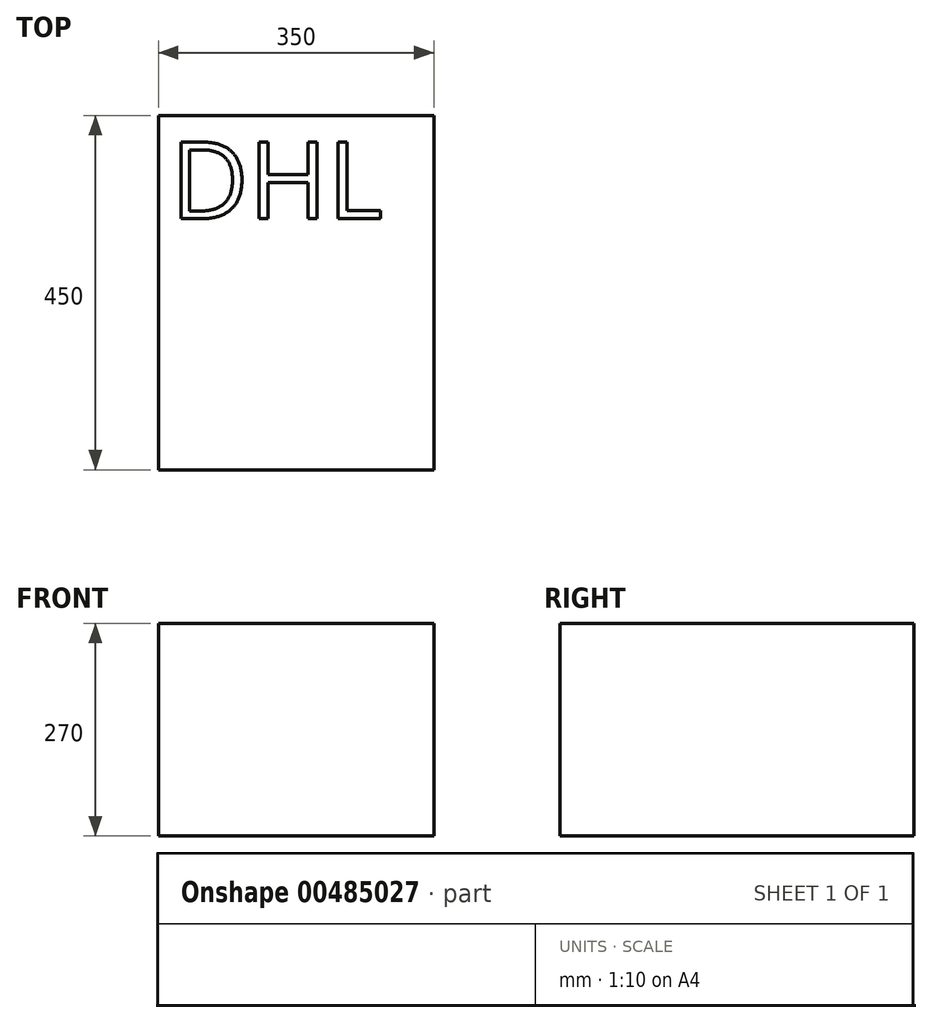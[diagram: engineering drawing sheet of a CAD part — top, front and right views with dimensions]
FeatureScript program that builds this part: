
annotation { "Feature Type Name" : "Feature", "Feature Type Description" : "" }
export const myFeature = defineFeature(function(context is Context, id is Id, definition is map)
    precondition{}
    {
        {
            var Q0;
            Q0=qCreatedBy(makeId("Top.planeOp"),FACE);
            var sketch = newSketch(context, id + "F0", { "sketchPlane" : qUnion([Q0])});
            skLineSegment(sketch, "E0.bottom", {"start": v(175, -225) * mm, "end": v(-175, -225) * mm});
            skLineSegment(sketch, "E0.top", {"start": v(175, 225) * mm, "end": v(-175, 225) * mm});
            skLineSegment(sketch, "E0.left", {"start": v(175, -225) * mm, "end": v(175, 225) * mm});
            skLineSegment(sketch, "E0.right", {"start": v(-175, -225) * mm, "end": v(-175, 225) * mm});
            skPoint(sketch, "E0.middle", {"position": v(0, 0) * mm});
            skSolve(sketch);
        }
        {
            var Q0;
            Q0=makeQuery(id+"F0.imprint","IMPRINT",FACE,{"disambiguationData":[TD([[makeQuery(id+"F0.imprint","IMPRINT",EDGE,{"derivedFrom":sQuery(id+"F0.wireOp",EDGE,"E0.bottom")}),-1.0]])]});
            extrude(context, id + "F1", {"entities" : qUnion([Q0]), "depth" : 270 * mm});
        }
        {
            var Q0;
            Q0=makeQuery(id+"F1.opExtrude","CAP_FACE",FACE,{"disambiguationData":[OSD([sQuery(id+"F0.wireOp",EDGE,"E0.bottom"),sQuery(id+"F0.wireOp",EDGE,"E0.top"),sQuery(id+"F0.wireOp",EDGE,"E0.left"),sQuery(id+"F0.wireOp",EDGE,"E0.right")])],"isStart":false});
            var sketch = newSketch(context, id + "F2", { "sketchPlane" : qUnion([Q0])});
            skSolve(sketch);
        }
        {
            var Q0;
            Q0=makeQuery(id+"F2.imprint","IMPRINT",FACE,{"disambiguationData":[TD([[makeQuery(id+"F2.imprint","IMPRINT",EDGE,{"derivedFrom":makeQuery(id+"F1.opExtrude","CAP_EDGE",EDGE,{"disambiguationData":[OSD([sQuery(id+"F0.wireOp",EDGE,"E0.bottom")])],"isStart":false})}),-1.0]])]});
            var sketch = newSketch(context, id + "F3", { "sketchPlane" : qUnion([Q0])});
            skText(sketch, "E1", { "text": "DHL", "fontName": "OpenSans-Regular.ttf"});
            const initialGuessF3  = {"E1": [-0.15963, 0.0941, 1, 0, 0.09794]};
            skSetInitialGuess(sketch, initialGuessF3);
            skSolve(sketch);
        }
        {
            var Q0;
            Q0 = qSketchRegion(id + "F3", true);
            extrude(context, id + "F4", {"entities" : qUnion([Q0]), "operationType" : NewBodyOperationType.REMOVE, "oppositeDirection" : true, "depth" : 1 * mm});
        }
    });
